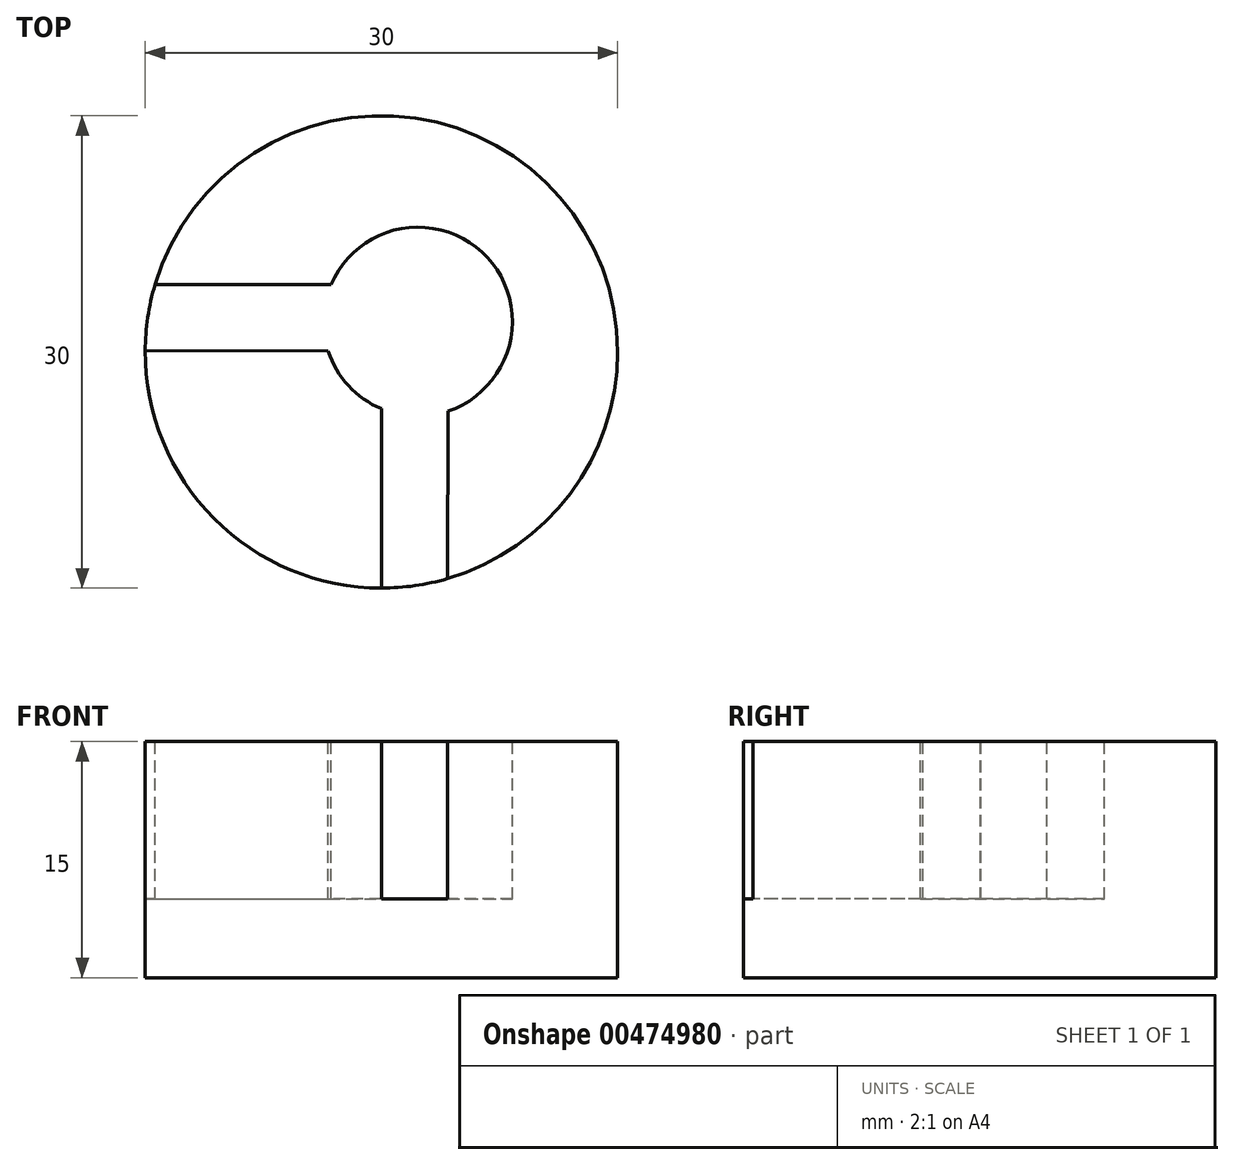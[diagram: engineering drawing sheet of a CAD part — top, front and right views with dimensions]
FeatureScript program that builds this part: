
annotation { "Feature Type Name" : "Feature", "Feature Type Description" : "" }
export const myFeature = defineFeature(function(context is Context, id is Id, definition is map)
    precondition{}
    {
        {
            var Q0;
            Q0=qCreatedBy(makeId("Top.planeOp"),FACE);
            var sketch = newSketch(context, id + "F0", { "sketchPlane" : qUnion([Q0])});
            skCircle(sketch, "E0", {"center": v(0, 0) * mm, "radius": 15 * mm});
            skSolve(sketch);
        }
        {
            var Q0;
            Q0 = qSketchRegion(id + "F0", true);
            extrude(context, id + "F1", {"entities" : qUnion([Q0]), "oppositeDirection" : true, "depth" : 15 * mm});
        }
        {
            var Q0;
            Q0=qCreatedBy(makeId("Top.planeOp"),FACE);
            var sketch = newSketch(context, id + "F2", { "sketchPlane" : qUnion([Q0])});
            skLineSegment(sketch, "E1.bottom", {"start": v(-15.76, 4.28) * mm, "end": v(4.24, 4.28) * mm});
            skLineSegment(sketch, "E1.left", {"start": v(-15.76, 4.28) * mm, "end": v(-15.76, 0.08) * mm});
            skLineSegment(sketch, "E2.top", {"start": v(0, -19.96) * mm, "end": v(4.2, -19.96) * mm});
            skLineSegment(sketch, "E2.left", {"start": v(0, 0.04) * mm, "end": v(0, -19.96) * mm});
            skLineSegment(sketch, "E3", {"start": v(-15.76, 0.08) * mm, "end": v(0, 0.04) * mm});
            skLineSegment(sketch, "E4", {"start": v(4.24, 4.28) * mm, "end": v(4.2, -19.96) * mm});
            skSolve(sketch);
        }
        {
            var Q0;
            Q0 = qSketchRegion(id + "F2", true);
            extrude(context, id + "F3", {"entities" : qUnion([Q0]), "operationType" : NewBodyOperationType.REMOVE, "endBound" : BoundingType.SYMMETRIC, "oppositeDirection" : true, "depth" : 20 * mm});
        }
        {
            var Q0;
            Q0=qCreatedBy(makeId("Top.planeOp"),FACE);
            var sketch = newSketch(context, id + "F4", { "sketchPlane" : qUnion([Q0])});
            skCircle(sketch, "E5", {"center": v(2.32, 1.92) * mm, "radius": 6 * mm});
            skSolve(sketch);
        }
        {
            var Q0;
            Q0 = qSketchRegion(id + "F4", true);
            extrude(context, id + "F5", {"entities" : qUnion([Q0]), "operationType" : NewBodyOperationType.REMOVE, "endBound" : BoundingType.SYMMETRIC, "oppositeDirection" : true, "depth" : 20 * mm});
        }
    });
